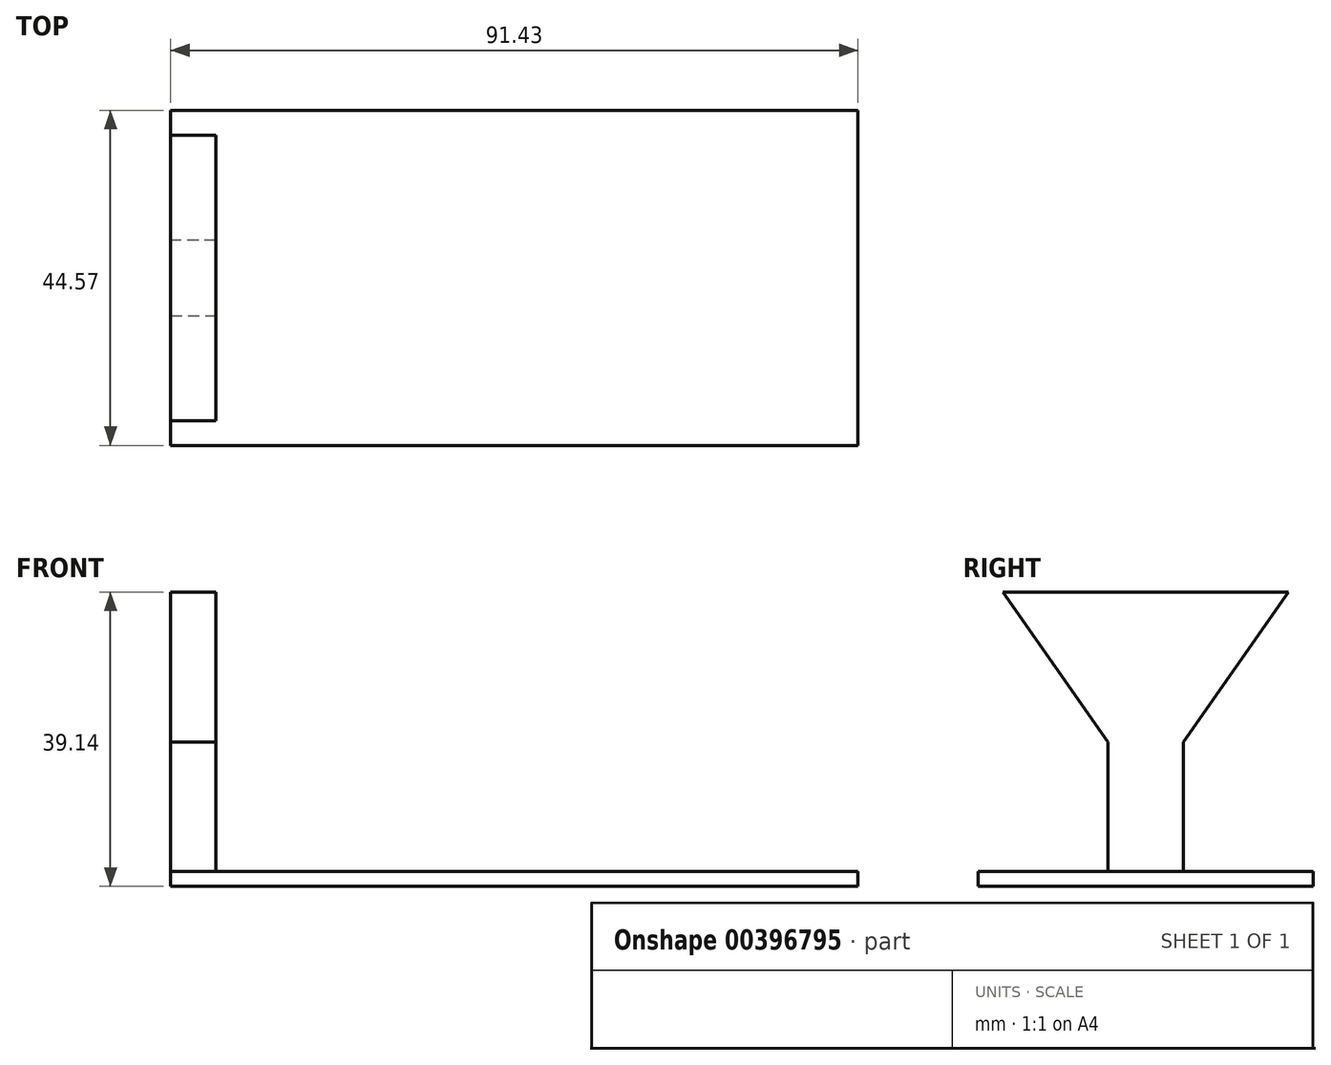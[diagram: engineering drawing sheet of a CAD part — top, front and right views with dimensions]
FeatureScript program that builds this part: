
annotation { "Feature Type Name" : "Feature", "Feature Type Description" : "" }
export const myFeature = defineFeature(function(context is Context, id is Id, definition is map)
    precondition{}
    {
        {
            assignVariable(context, id + "F0", {"name" : "SizeDivision", "anyValue" : 17.5});
        }
        {
            var Q0;
            Q0=qCreatedBy(makeId("Top.planeOp"),FACE);
            var sketch = newSketch(context, id + "F1", { "sketchPlane" : qUnion([Q0])});
            skLineSegment(sketch, "E0.bottom", {"start": v(0, 0) * mm, "end": v(91.43, 0) * mm});
            skLineSegment(sketch, "E0.top", {"start": v(0, -44.57) * mm, "end": v(91.43, -44.57) * mm});
            skLineSegment(sketch, "E0.left", {"start": v(0, 0) * mm, "end": v(0, -44.57) * mm});
            skLineSegment(sketch, "E0.right", {"start": v(91.43, 0) * mm, "end": v(91.43, -44.57) * mm});
            skLineSegment(sketch, "E1", {"start": v(45.71, -44.57) * mm, "end": v(45.71, 0) * mm, "construction": true});
            skSolve(sketch);
        }
        {
            var Q0;
            Q0 = qSketchRegion(id + "F1", true);
            extrude(context, id + "F2", {"entities" : qUnion([Q0]), "depth" : 2 * mm});
        }
        {
            var Q0;
            Q0=makeQuery(id+"F2.opExtrude","CAP_FACE",FACE,{"disambiguationData":[OSD([sQuery(id+"F1.wireOp",EDGE,"E0.bottom"),sQuery(id+"F1.wireOp",EDGE,"E0.top"),sQuery(id+"F1.wireOp",EDGE,"E0.left"),sQuery(id+"F1.wireOp",EDGE,"E0.right")])],"isStart":false});
            var sketch = newSketch(context, id + "F3", { "sketchPlane" : qUnion([Q0])});
            skLineSegment(sketch, "E2.bottom", {"start": v(0, -17.29) * mm, "end": v(6, -17.29) * mm});
            skLineSegment(sketch, "E2.top", {"start": v(0, -27.29) * mm, "end": v(6, -27.29) * mm});
            skLineSegment(sketch, "E2.left", {"start": v(0, -17.29) * mm, "end": v(0, -27.29) * mm});
            skLineSegment(sketch, "E2.right", {"start": v(6, -17.29) * mm, "end": v(6, -27.29) * mm});
            skLineSegment(sketch, "E3", {"start": v(91.43, -22.29) * mm, "end": v(0, -22.29) * mm, "construction": true});
            skSolve(sketch);
        }
        {
            var Q0;
            Q0=makeQuery(id+"F3.imprint","IMPRINT",FACE,{"disambiguationData":[TD([[makeQuery(id+"F3.imprint","IMPRINT",EDGE,{"derivedFrom":sQuery(id+"F3.wireOp",EDGE,"E2.bottom")}),-1.0]])]});
            extrude(context, id + "F4", {"entities" : qUnion([Q0]), "operationType" : NewBodyOperationType.ADD, "depth" : (650 / getVariable(context, 'SizeDivision')) * mm});
        }
        {
            var Q0;
            Q0=makeQuery(id+"F4.opExtrude","CAP_FACE",FACE,{"disambiguationData":[OSD([sQuery(id+"F3.wireOp",EDGE,"E2.bottom"),sQuery(id+"F3.wireOp",EDGE,"E2.top"),sQuery(id+"F3.wireOp",EDGE,"E2.left"),sQuery(id+"F3.wireOp",EDGE,"E2.right")])],"isStart":false});
            var sketch = newSketch(context, id + "F5", { "sketchPlane" : qUnion([Q0])});
            skLineSegment(sketch, "E4", {"start": v(0, 0) * mm, "end": v(6, 0) * mm});
            skLineSegment(sketch, "E5", {"start": v(6, 0) * mm, "end": v(6, -44.57) * mm});
            skLineSegment(sketch, "E6", {"start": v(6, -44.57) * mm, "end": v(0, -44.57) * mm});
            skLineSegment(sketch, "E7", {"start": v(0, -44.57) * mm, "end": v(0, 0) * mm});
            skSolve(sketch);
        }
        {
            var Q0;
            Q0 = qSketchRegion(id + "F5", true);
            extrude(context, id + "F6", {"entities" : qUnion([Q0]), "operationType" : NewBodyOperationType.ADD, "oppositeDirection" : true, "depth" : 20 * mm});
        }
        {
            var Q0;
            Q0=makeQuery(id+"F6.opExtrude","CAP_EDGE",EDGE,{"disambiguationData":[OSD([sQuery(id+"F5.wireOp",EDGE,"E6")])],"isStart":false});
            var Q1;
            Q1=makeQuery(id+"F6.opExtrude","CAP_EDGE",EDGE,{"disambiguationData":[OSD([sQuery(id+"F5.wireOp",EDGE,"E4")])],"isStart":false});
            chamfer(context, id + "F7", {"entities" : qUnion([Q0, Q1]), "chamferType" : ChamferType.OFFSET_ANGLE, "width" : 17.3 * mm, "oppositeDirection" : false, "angle" : 55 * degree, "tangentPropagation" : true});
        }
        {
            var Q0;
            Q0=makeQuery(id+"F2.opExtrude","CAP_EDGE",EDGE,{"disambiguationData":[OSD([sQuery(id+"F1.wireOp",EDGE,"E0.top")])],"isStart":false});
            cPoint(context, id + "F8", {"entities" : qUnion([Q0]), "parameter" : 0.5});
        }
        {
            var Q0;
            Q0=qCreatedBy(makeId("Right.planeOp"),FACE);
            var Q1;
            Q1 = qCreatedBy(id + "F8" ,VERTEX);
            cPlane(context, id + "F9", {"entities" : qUnion([Q0, Q1]), "cplaneType" : CPlaneType.PLANE_POINT, "offset" : 25 * mm, "width" : 150 * mm, "height" : 150 * mm});
        }
    });
